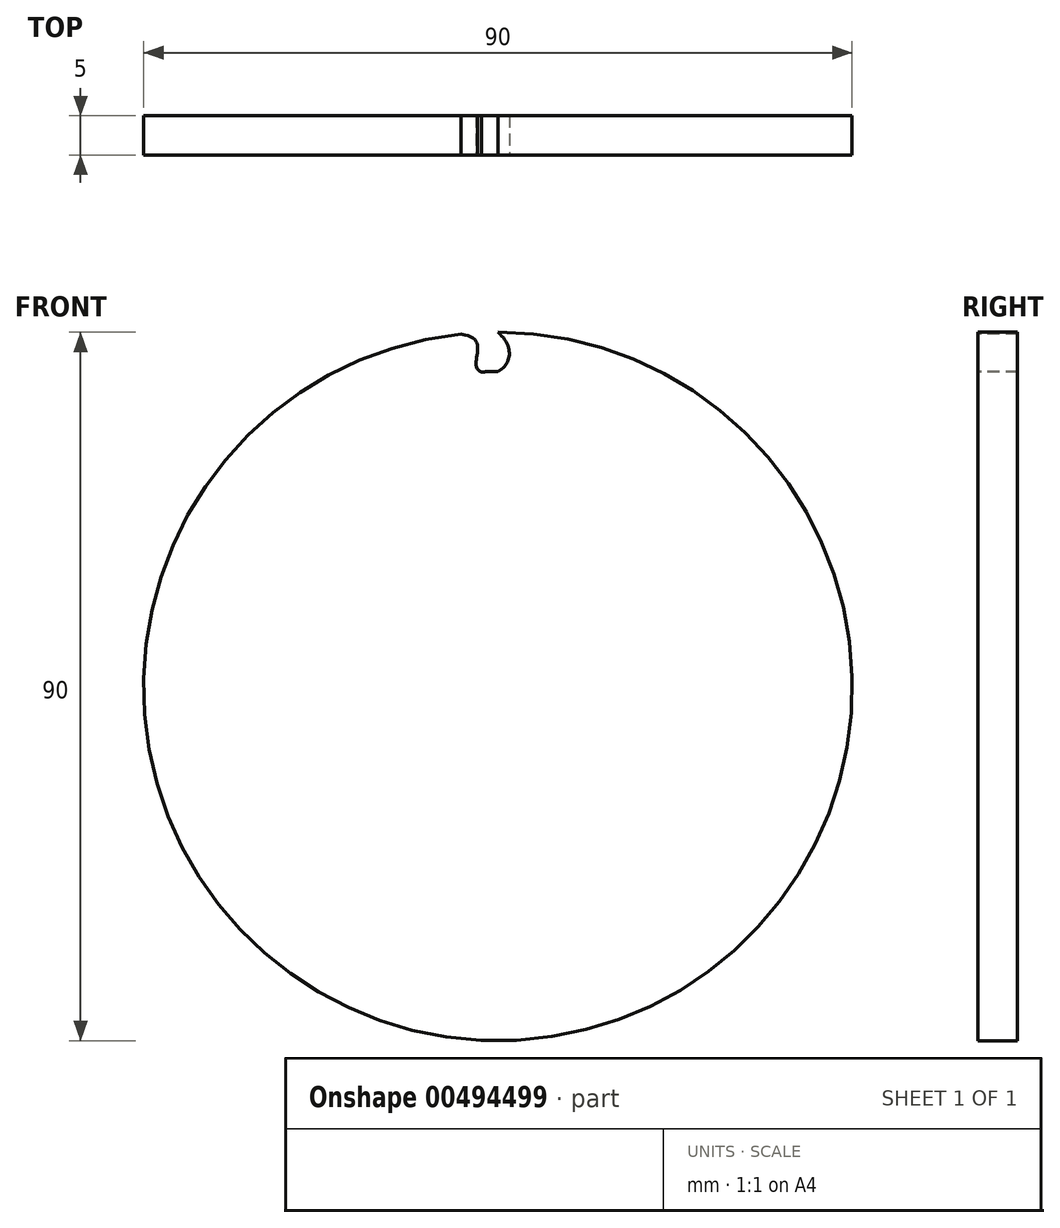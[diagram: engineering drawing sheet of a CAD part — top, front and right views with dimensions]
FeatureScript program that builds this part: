
annotation { "Feature Type Name" : "Feature", "Feature Type Description" : "" }
export const myFeature = defineFeature(function(context is Context, id is Id, definition is map)
    precondition{}
    {
        {
            var Q0;
            Q0=qCreatedBy(makeId("Front.planeOp"),FACE);
            var sketch = newSketch(context, id + "F0", { "sketchPlane" : qUnion([Q0])});
            skCircle(sketch, "E0", {"center": v(0, 0) * mm, "radius": 45 * mm});
            skSolve(sketch);
        }
        {
            var Q0;
            Q0 = qSketchRegion(id + "F0", true);
            extrude(context, id + "F1", {"entities" : qUnion([Q0]), "depth" : 5 * mm, "offsetDistance" : 25 * mm});
        }
        {
            var Q0;
            Q0=makeQuery(id+"F1.opExtrude","CAP_FACE",FACE,{"disambiguationData":[OSD([sQuery(id+"F0.wireOp",EDGE,"E0")])],"isStart":false});
            var sketch = newSketch(context, id + "F2", { "sketchPlane" : qUnion([Q0])});
            skCircle(sketch, "E1", {"center": v(0, 0) * mm, "radius": 40 * mm});
            skFitSpline(sketch, "E2", {"points": [v(0, 40) * mm, v(0, 45) * mm], "startDerivative": vector(5.57, 3.1) * mm, "endDerivative": vector(-6.06, 5.32) * mm});
            skFitSpline(sketch, "E3", {"points": [v(0, 45) * mm, v(6.47, 39.47) * mm], "startDerivative": vector(17.68, 0.6) * mm, "endDerivative": vector(19.42, -9.32) * mm});
            skFitSpline(sketch, "E4", {"points": [v(-4.71, 44.75) * mm, v(-2.1, 39.95) * mm], "startDerivative": vector(12.64, -1.64) * mm, "endDerivative": vector(6.2, -2.65) * mm});
            skSolve(sketch);
        }
        {
            var Q0;
            {var subQ0=sQuery(id+"F2.wireOp",EDGE,"E3");var subQ1=makeQuery(id+"F1.opExtrude","CAP_EDGE",EDGE,{"disambiguationData":[OSD([sQuery(id+"F0.wireOp",EDGE,"E0")])],"isStart":false});var subQ3=makeQuery(id+"F2.imprint","INTERSECT",VERTEX,{"derivedFrom":[subQ1,subQ0]});Q0=makeQuery(id+"F2.imprint","IMPRINT",FACE,{"disambiguationData":[TD([[makeQuery(id+"F2.imprint","IMPRINT",EDGE,{"disambiguationData":[TD([[subQ3,1.0]])],"derivedFrom":subQ0}),-1.0]])]});}
            var Q1;
            {var subQ0=sQuery(id+"F2.wireOp",EDGE,"E2");Q1=makeQuery(id+"F2.imprint","IMPRINT",FACE,{"disambiguationData":[TD([[makeQuery(id+"F2.imprint","IMPRINT",EDGE,{"derivedFrom":subQ0}),1.0]])]});}
            extrude(context, id + "F3", {"entities" : qUnion([Q0, Q1]), "operationType" : NewBodyOperationType.REMOVE, "oppositeDirection" : true, "depth" : 25 * mm, "offsetDistance" : 25 * mm});
        }
        {
            var Q0;
            Q0=makeQuery(id+"F1.opExtrude","CAP_FACE",FACE,{"disambiguationData":[OSD([sQuery(id+"F0.wireOp",EDGE,"E0")])],"isStart":false});
            var sketch = newSketch(context, id + "F4", { "sketchPlane" : qUnion([Q0])});
            skCircle(sketch, "E5", {"center": v(0, 0) * mm, "radius": 22.93 * mm});
            skSolve(sketch);
        }
    });
